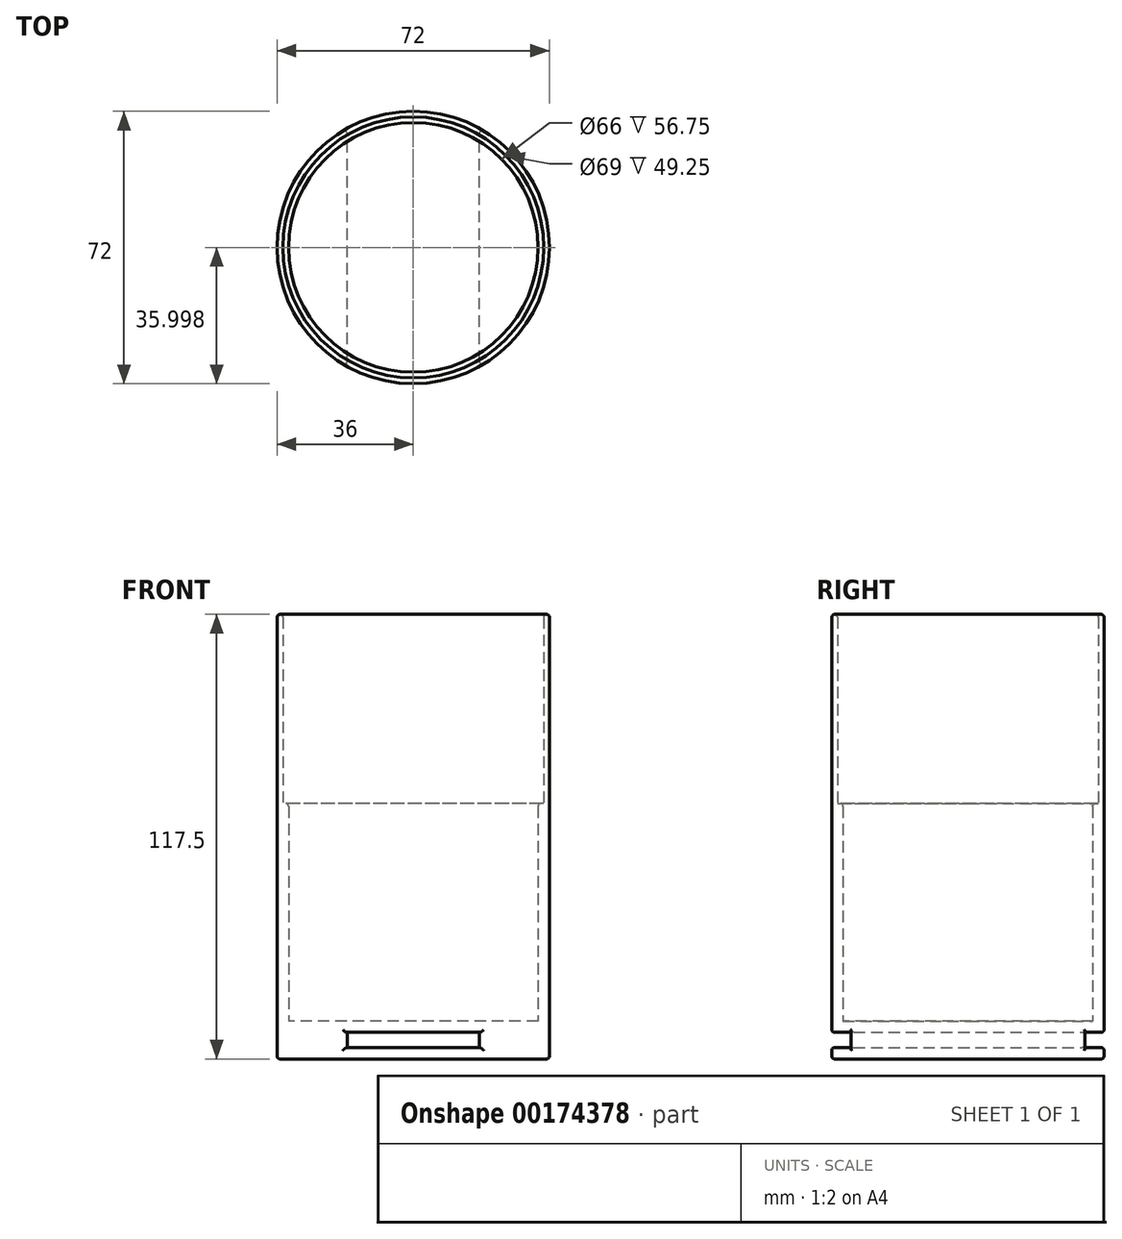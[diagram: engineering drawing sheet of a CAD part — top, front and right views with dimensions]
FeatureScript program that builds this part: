
annotation { "Feature Type Name" : "Feature", "Feature Type Description" : "" }
export const myFeature = defineFeature(function(context is Context, id is Id, definition is map)
    precondition{}
    {
        {
            var Q0;
            Q0=qCreatedBy(makeId("Top.planeOp"),FACE);
            var sketch = newSketch(context, id + "F0", { "sketchPlane" : qUnion([Q0])});
            skCircle(sketch, "E0.0", {"center": v(0, -2.8) * mm, "radius": 36 * mm});
            skLineSegment(sketch, "E1", {"start": v(0, 33.2) * mm, "end": v(0, -38.8) * mm});
            skLineSegment(sketch, "E2", {"start": v(0, -2.8) * mm, "end": v(-36, -2.8) * mm});
            skLineSegment(sketch, "E3", {"start": v(0, -2.8) * mm, "end": v(36, -2.8) * mm});
            skSolve(sketch);
        }
        {
            var Q0;
            Q0=qSketchRegion(id+"F0",true);
            var Q1;
            Q1=makeQuery(id+"F0.imprint","IMPRINT",FACE,{"disambiguationData":[TD([[makeQuery(id+"F0.imprint","IMPRINT",EDGE,{"derivedFrom":sQuery(id+"F0.wireOp",EDGE,"E0.0")}),1.0]])]});
            extrude(context, id + "F1", {"entities" : qUnion([Q0, Q1]), "depth" : 10 * mm});
        }
        {
            var Q0;
            Q0=makeQuery(id+"F1.opExtrude","CAP_FACE",FACE,{"disambiguationData":[OSD([sQuery(id+"F0.wireOp",EDGE,"E0.0")])],"isStart":false});
            var sketch = newSketch(context, id + "F2", { "sketchPlane" : qUnion([Q0])});
            skCircle(sketch, "E4.0", {"center": v(0, -2.8) * mm, "radius": 33 * mm});
            skCircle(sketch, "E5.0", {"center": v(0, -2.8) * mm, "radius": 36 * mm});
            skSolve(sketch);
        }
        {
            var Q0;
            Q0=qCreatedBy(makeId("Front.planeOp"),FACE);
            var sketch = newSketch(context, id + "F3", { "sketchPlane" : qUnion([Q0])});
            skLineSegment(sketch, "E6", {"start": v(-42.08, 0) * mm, "end": v(47.5, 0) * mm});
            skLineSegment(sketch, "E7.0", {"start": v(-17.5, 3) * mm, "end": v(17.5, 3) * mm});
            skLineSegment(sketch, "E8.0", {"start": v(-17.5, 7) * mm, "end": v(17.5, 7) * mm});
            skLineSegment(sketch, "E9.0", {"start": v(17.5, 3) * mm, "end": v(17.5, 7) * mm});
            skLineSegment(sketch, "E10.0", {"start": v(-17.5, 3) * mm, "end": v(-17.5, 7) * mm});
            skSolve(sketch);
        }
        {
            var Q0;
            Q0=qSketchRegion(id+"F3",true);
            extrude(context, id + "F4", {"entities" : qUnion([Q0]), "operationType" : NewBodyOperationType.REMOVE, "endBound" : BoundingType.THROUGH_ALL, "depth" : 44.2 * mm, "hasSecondDirection" : true, "secondDirectionOppositeDirection" : true, "secondDirectionDepth" : 36.8 * mm});
        }
        {
            var Q0;
            Q0 = qSketchRegion(id + "F2", true);
            extrude(context, id + "F5", {"entities" : qUnion([Q0]), "operationType" : NewBodyOperationType.ADD, "depth" : 57.5 * mm});
        }
        {
            var Q0;
            Q0=makeQuery(id+"F5.opExtrude","CAP_FACE",FACE,{"disambiguationData":[OSD([sQuery(id+"F2.wireOp",EDGE,"E4.0"),sQuery(id+"F2.wireOp",EDGE,"E5.0")])],"isStart":false});
            var sketch = newSketch(context, id + "F6", { "sketchPlane" : qUnion([Q0])});
            skCircle(sketch, "E11", {"center": v(0, -2.8) * mm, "radius": 36 * mm});
            skCircle(sketch, "E12.0", {"center": v(0, -2.8) * mm, "radius": 34.5 * mm});
            skSolve(sketch);
        }
        {
            var Q0;
            Q0 = qSketchRegion(id + "F6", true);
            extrude(context, id + "F7", {"entities" : qUnion([Q0]), "operationType" : NewBodyOperationType.ADD, "depth" : 50 * mm});
        }
        {
            var Q0;
            Q0=makeQuery(id+"F7.opExtrude","CAP_EDGE",EDGE,{"disambiguationData":[OSD([sQuery(id+"F6.wireOp",EDGE,"E12.0")])],"isStart":false});
            var Q1;
            Q1=makeQuery(id+"F7.opExtrude","CAP_EDGE",EDGE,{"disambiguationData":[OSD([sQuery(id+"F6.wireOp",EDGE,"E11")])],"isStart":false});
            var Q2;
            Q2=makeQuery(id+"F5.opExtrude","CAP_EDGE",EDGE,{"disambiguationData":[OSD([sQuery(id+"F2.wireOp",EDGE,"E4.0")])],"isStart":false});
            var Q3;
            Q3=makeQuery(id+"F4.boolean.opBoolean","INTERSECT",EDGE,{"disambiguationData":[OD(0.0)],"derivedFrom":[makeQuery(id+"F1.opExtrude","SWEPT_FACE",FACE,{"disambiguationData":[OSD([sQuery(id+"F0.wireOp",EDGE,"E0.0")])]}),makeQuery(id+"F4.opExtrude","SWEPT_FACE",FACE,{"disambiguationData":[OSD([sQuery(id+"F3.wireOp",EDGE,"E8.0")])]})]});
            var Q4;
            Q4=makeQuery(id+"F4.boolean.opBoolean","INTERSECT",EDGE,{"disambiguationData":[OD(0.0)],"derivedFrom":[makeQuery(id+"F1.opExtrude","SWEPT_FACE",FACE,{"disambiguationData":[OSD([sQuery(id+"F0.wireOp",EDGE,"E0.0")])]}),makeQuery(id+"F4.opExtrude","SWEPT_FACE",FACE,{"disambiguationData":[OSD([sQuery(id+"F3.wireOp",EDGE,"E10.0")])]})]});
            var Q5;
            Q5=makeQuery(id+"F4.boolean.opBoolean","INTERSECT",EDGE,{"disambiguationData":[OD(0.0)],"derivedFrom":[makeQuery(id+"F1.opExtrude","SWEPT_FACE",FACE,{"disambiguationData":[OSD([sQuery(id+"F0.wireOp",EDGE,"E0.0")])]}),makeQuery(id+"F4.opExtrude","SWEPT_FACE",FACE,{"disambiguationData":[OSD([sQuery(id+"F3.wireOp",EDGE,"E7.0")])]})]});
            var Q6;
            Q6=makeQuery(id+"F4.boolean.opBoolean","INTERSECT",EDGE,{"disambiguationData":[OD(0.0)],"derivedFrom":[makeQuery(id+"F1.opExtrude","SWEPT_FACE",FACE,{"disambiguationData":[OSD([sQuery(id+"F0.wireOp",EDGE,"E0.0")])]}),makeQuery(id+"F4.opExtrude","SWEPT_FACE",FACE,{"disambiguationData":[OSD([sQuery(id+"F3.wireOp",EDGE,"E9.0")])]})]});
            var Q7;
            Q7=makeQuery(id+"F1.opExtrude","CAP_EDGE",EDGE,{"disambiguationData":[OSD([sQuery(id+"F0.wireOp",EDGE,"E0.0")])],"isStart":true});
            var Q8;
            Q8=makeQuery(id+"F4.boolean.opBoolean","INTERSECT",EDGE,{"disambiguationData":[OD(1.0)],"derivedFrom":[makeQuery(id+"F1.opExtrude","SWEPT_FACE",FACE,{"disambiguationData":[OSD([sQuery(id+"F0.wireOp",EDGE,"E0.0")])]}),makeQuery(id+"F4.opExtrude","SWEPT_FACE",FACE,{"disambiguationData":[OSD([sQuery(id+"F3.wireOp",EDGE,"E8.0")])]})]});
            var Q9;
            Q9=makeQuery(id+"F4.boolean.opBoolean","INTERSECT",EDGE,{"disambiguationData":[OD(1.0)],"derivedFrom":[makeQuery(id+"F1.opExtrude","SWEPT_FACE",FACE,{"disambiguationData":[OSD([sQuery(id+"F0.wireOp",EDGE,"E0.0")])]}),makeQuery(id+"F4.opExtrude","SWEPT_FACE",FACE,{"disambiguationData":[OSD([sQuery(id+"F3.wireOp",EDGE,"E9.0")])]})]});
            var Q10;
            Q10=makeQuery(id+"F4.boolean.opBoolean","INTERSECT",EDGE,{"disambiguationData":[OD(1.0)],"derivedFrom":[makeQuery(id+"F1.opExtrude","SWEPT_FACE",FACE,{"disambiguationData":[OSD([sQuery(id+"F0.wireOp",EDGE,"E0.0")])]}),makeQuery(id+"F4.opExtrude","SWEPT_FACE",FACE,{"disambiguationData":[OSD([sQuery(id+"F3.wireOp",EDGE,"E7.0")])]})]});
            var Q11;
            Q11=makeQuery(id+"F4.boolean.opBoolean","INTERSECT",EDGE,{"disambiguationData":[OD(1.0)],"derivedFrom":[makeQuery(id+"F1.opExtrude","SWEPT_FACE",FACE,{"disambiguationData":[OSD([sQuery(id+"F0.wireOp",EDGE,"E0.0")])]}),makeQuery(id+"F4.opExtrude","SWEPT_FACE",FACE,{"disambiguationData":[OSD([sQuery(id+"F3.wireOp",EDGE,"E10.0")])]})]});
            fillet(context, id + "F8", {"entities" : qUnion([Q0, Q1, Q2, Q3, Q4, Q5, Q6, Q7, Q8, Q9, Q10, Q11]), "radius" : .75 * mm, "tangentPropagation" : true, "allowEdgeOverflow" : false});
        }
    });
